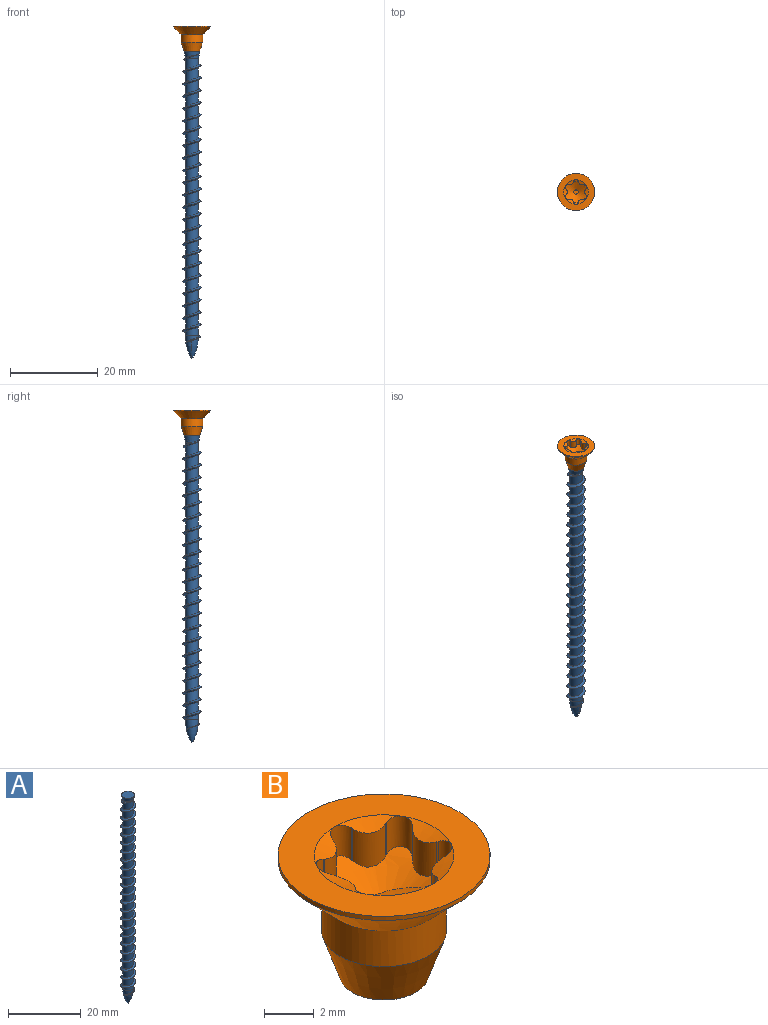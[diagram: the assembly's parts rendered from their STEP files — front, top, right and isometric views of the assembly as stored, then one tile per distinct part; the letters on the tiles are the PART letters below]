
ASSEMBLY  parts=2 mates=1
PART A: 13 faces, bbox 4.7x5.1x70 mm
  f0: plane 3.56x3.56mm, normal (0,0,1), area 9.9mm2, adj f1
  f1: cone r=25.4mm half-angle=11.7deg, axis (0,0,1), area 49mm2, adj f0
  f2: revolved ~3.99x2.82mm, area -5.3mm2, adj f3,f12
  f3: revolved ~5.21x2.95mm, area 14.8mm2, adj f2,f4,f12
  f4: revolved ~2.95x2.95mm, area 9.4mm2, adj f3,f5,f11
  f5: bspline ~3.91x3.71mm, area 3.3mm2, adj f4,f6,f11,f12
  f6: bspline ~61.76x5.07mm, area 171.5mm2, adj f5,f7,f10,f11
  f7: bspline ~3.98x3.94mm, area 3.8mm2, adj f6,f8,f9,f11
  f8: cone r=25.4mm half-angle=11.7deg, axis (0,0,1), area 2.4mm2, adj f7,f9,f11
  f9: bspline ~3.99x3.95mm, area 4mm2, adj f7,f8,f10,f11
  f10: bspline ~61.76x4.12mm, area 171.5mm2, adj f6,f9,f11,f12
  f11: cylinder r=1.47mm len=63.36mm, axis (0,0,-1), area 448.8mm2, adj f4,f5,f6,f7,f8,f9,f10
  f12: bspline ~3.92x3.72mm, area 3.2mm2, adj f2,f3,f5,f10
PART B: 38 faces, bbox 8.5x8.5x5.9 mm
  f0: plane 8.5x8.5mm, normal (0,0,1), area 32.1mm2, adj f1,f2,f3,f4,f5,f6,f33
  f1: cone r=2.8mm half-angle=70deg, axis (0,0,1), area 1.2mm2, adj f0,f9,f10,f11,f12,f32
  f2: cone r=2.8mm half-angle=70deg, axis (0,0,1), area 1.2mm2, adj f0,f12,f13,f14,f15,f16
  f3: cone r=2.8mm half-angle=70deg, axis (0,0,1), area 1.2mm2, adj f0,f16,f17,f18,f19,f20
  f4: cone r=2.8mm half-angle=70deg, axis (0,0,1), area 1.2mm2, adj f0,f20,f21,f22,f23,f24
  f5: cone r=2.8mm half-angle=70deg, axis (0,0,1), area 1.2mm2, adj f0,f24,f25,f26,f27,f28
  f6: cone r=2.8mm half-angle=70deg, axis (0,0,1), area 1.2mm2, adj f0,f28,f29,f30,f31,f32
  f7: plane 1x1mm, normal (0,0,1), area 0.8mm2, adj f8
  f8: cone r=2.8mm half-angle=60deg, axis (0,0,1), area 19.8mm2, adj f7,f9,f10,f11,f12,f13,f14,f15
  f9: plane 1.6x0.04mm, normal (0.26,-0.97,0), area 0.1mm2, adj f1,f8,f10,f32
  f10: cylinder r=0.98mm len=1.81mm, axis (0,0,1), area 2.5mm2, adj f1,f8,f9,f11
  f11: plane 1.6x0.04mm, normal (-0.97,-0.26,0), area 0.1mm2, adj f1,f8,f10,f12
  f12: cylinder r=0.56mm len=1.7mm, axis (0,0,1), area 2.2mm2, adj f1,f2,f8,f11,f13
  f13: plane 1.6x0.04mm, normal (0.97,-0.26,0), area 0.1mm2, adj f2,f8,f12,f14
  f14: cylinder r=0.98mm len=1.81mm, axis (0,0,1), area 2.5mm2, adj f2,f8,f13,f15
  f15: plane 1.6x0.04mm, normal (-0.26,-0.97,0), area 0.1mm2, adj f2,f8,f14,f16
  f16: cylinder r=0.56mm len=1.7mm, axis (0,0,1), area 2.2mm2, adj f2,f3,f8,f15,f17
  f17: plane 1.6x0.03mm, normal (0.71,0.71,0), area 0.1mm2, adj f3,f8,f16,f18
  f18: cylinder r=0.98mm len=1.81mm, axis (0,0,1), area 2.5mm2, adj f3,f8,f17,f19
  f19: plane 1.6x0.03mm, normal (0.71,-0.71,0), area 0.1mm2, adj f3,f8,f18,f20
  f20: cylinder r=0.56mm len=1.7mm, axis (0,0,1), area 2.2mm2, adj f3,f4,f8,f19,f21
  f21: plane 1.6x0.04mm, normal (-0.26,0.97,0), area 0.1mm2, adj f4,f8,f20,f22
  f22: cylinder r=0.98mm len=1.81mm, axis (0,0,1), area 2.5mm2, adj f4,f8,f21,f23
  f23: plane 1.6x0.04mm, normal (0.97,0.26,0), area 0.1mm2, adj f4,f8,f22,f24
  f24: cylinder r=0.56mm len=1.7mm, axis (0,0,1), area 2.2mm2, adj f4,f5,f8,f23,f25
  f25: plane 1.6x0.04mm, normal (-0.97,0.26,0), area 0.1mm2, adj f5,f8,f24,f26
  f26: cylinder r=0.98mm len=1.81mm, axis (0,0,1), area 2.5mm2, adj f5,f8,f25,f27
  f27: plane 1.6x0.04mm, normal (0.26,0.97,0), area 0.1mm2, adj f5,f8,f26,f28
  f28: cylinder r=0.56mm len=1.7mm, axis (0,0,1), area 2.2mm2, adj f5,f6,f8,f27,f29
  f29: plane 1.6x0.03mm, normal (-0.71,-0.71,0), area 0.1mm2, adj f6,f8,f28,f30
  f30: cylinder r=0.98mm len=1.81mm, axis (0,0,1), area 2.5mm2, adj f6,f8,f29,f31
  f31: plane 1.6x0.03mm, normal (-0.71,0.71,0), area 0.1mm2, adj f6,f8,f30,f32
  f32: cylinder r=0.56mm len=1.7mm, axis (0,0,1), area 2.2mm2, adj f1,f6,f8,f9,f31
  f33: cylinder r=4.25mm len=8.5mm, axis (0,0,1), area 5.3mm2, adj f0,f37
  f34: plane 3.56x3.56mm, normal (0,0,-1), area 10mm2, adj f35
  f35: cone r=2.5mm half-angle=18.6deg, axis (0,0,1), area 30.4mm2, adj f34,f36
  f36: cylinder r=2.5mm len=5mm, axis (0,0,-1), area 27.6mm2, adj f35,f37
  f37: cone r=4.45mm half-angle=45deg, axis (0,0,1), area 52.5mm2, adj f33,f36
PLACE A t=(-54.74,-1.22,-42.35)mm
PLACE B t=(-54.74,-1.22,42.65)mm
MATE fastened A.f1 <-> B.f8  axis (0,0,1) through (-54.74,-1.22,42.65)mm
